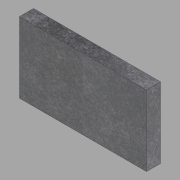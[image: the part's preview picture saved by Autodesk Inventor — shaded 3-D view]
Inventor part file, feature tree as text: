
AUTODESK INVENTOR PART (.ipt)
format: ipt  version: 2022.1 (Build 261234020, 234B)  size: 103,424 bytes
history: native  units: in
note: dims shown in document units (in); Inventor stores cm internally (conversion verified against a paired STEP export)
features: extrude x1, sketch x1
ambient origin geometry x8: Origin, YZ Plane, XZ Plane, XY Plane, X Axis, Y Axis, Z Axis, Center Point
bodies: Solid1 (feature_tree)
feature tree (2):
  extrude  "Extrusion1"  Depth=30.0in
  sketch  "Sketch1"  dims[d0=54.0in d1=30.0in d2=6.0in d3=0.0in]
